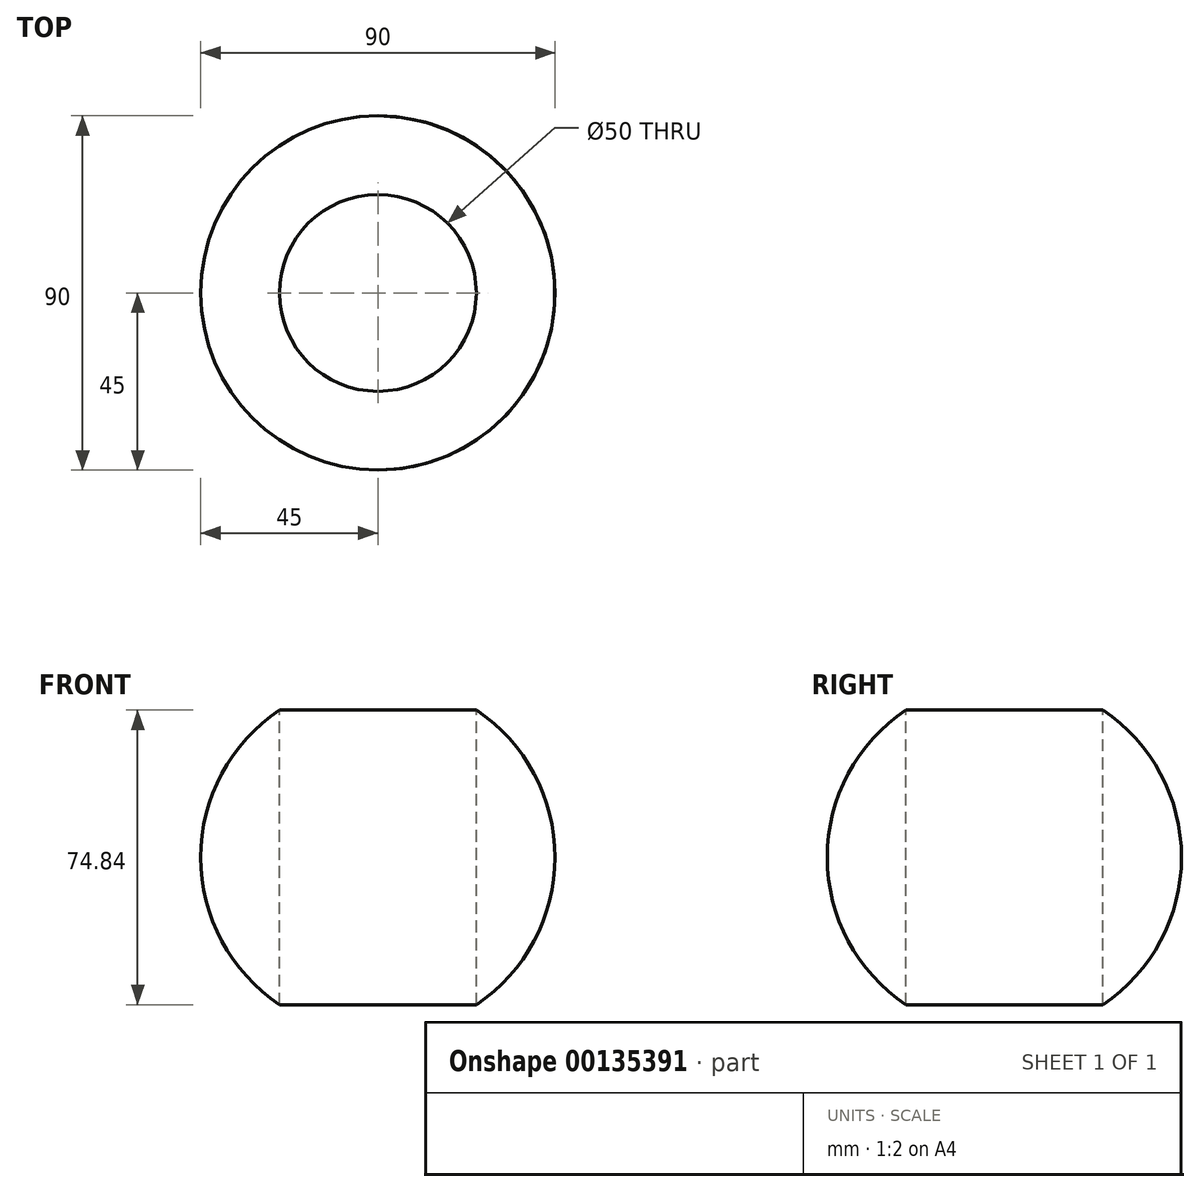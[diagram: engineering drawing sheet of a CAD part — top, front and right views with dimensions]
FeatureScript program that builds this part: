
annotation { "Feature Type Name" : "Feature", "Feature Type Description" : "" }
export const myFeature = defineFeature(function(context is Context, id is Id, definition is map)
    precondition{}
    {
        {
            var Q0;
            Q0=qCreatedBy(makeId("Top.planeOp"),FACE);
            var sketch = newSketch(context, id + "F0", { "sketchPlane" : qUnion([Q0])});
            skArc(sketch, "E0", {"start": v(0, -45) * mm, "mid": v(45, 0) * mm, "end": v(0, 45) * mm});
            skLineSegment(sketch, "E1", {"start": v(0, 0) * mm, "end": v(0, 59.7) * mm});
            skLineSegment(sketch, "E2", {"start": v(0, 0) * mm, "end": v(0, -65.4) * mm});
            skSolve(sketch);
        }
        {
            var Q0;
            Q0=qSketchRegion(id+"F0",true);
            var Q1;
            Q1=sQuery(id+"F0.wireOp",EDGE,"E1");
            revolve(context, id + "F1", {"entities" : qUnion([Q0]), "axis" : qUnion([Q1]), "revolveType" : RevolveType.FULL});
        }
        {
            var Q0;
            Q0=qCreatedBy(makeId("Top.planeOp"),FACE);
            var sketch = newSketch(context, id + "F2", { "sketchPlane" : qUnion([Q0])});
            skCircle(sketch, "E3", {"center": v(0, 0) * mm, "radius": 25 * mm});
            skSolve(sketch);
        }
        {
            var Q0;
            Q0=qSketchRegion(id+"F2",true);
            extrude(context, id + "F3", {"entities" : qUnion([Q0]), "operationType" : NewBodyOperationType.REMOVE, "endBound" : BoundingType.THROUGH_ALL, "oppositeDirection" : true, "depth" : 25 * mm});
        }
        {
            var Q0;
            Q0=makeQuery(id+"F3.boolean.opBoolean","COPY",FACE,{"derivedFrom":makeQuery(id+"F3.opExtrude","CAP_FACE",FACE,{"disambiguationData":[OSD([sQuery(id+"F2.wireOp",EDGE,"E3")])],"isStart":true})});
            extrude(context, id + "F4", {"entities" : qUnion([Q0]), "operationType" : NewBodyOperationType.REMOVE, "endBound" : BoundingType.THROUGH_ALL, "oppositeDirection" : true, "depth" : 25 * mm});
        }
    });
